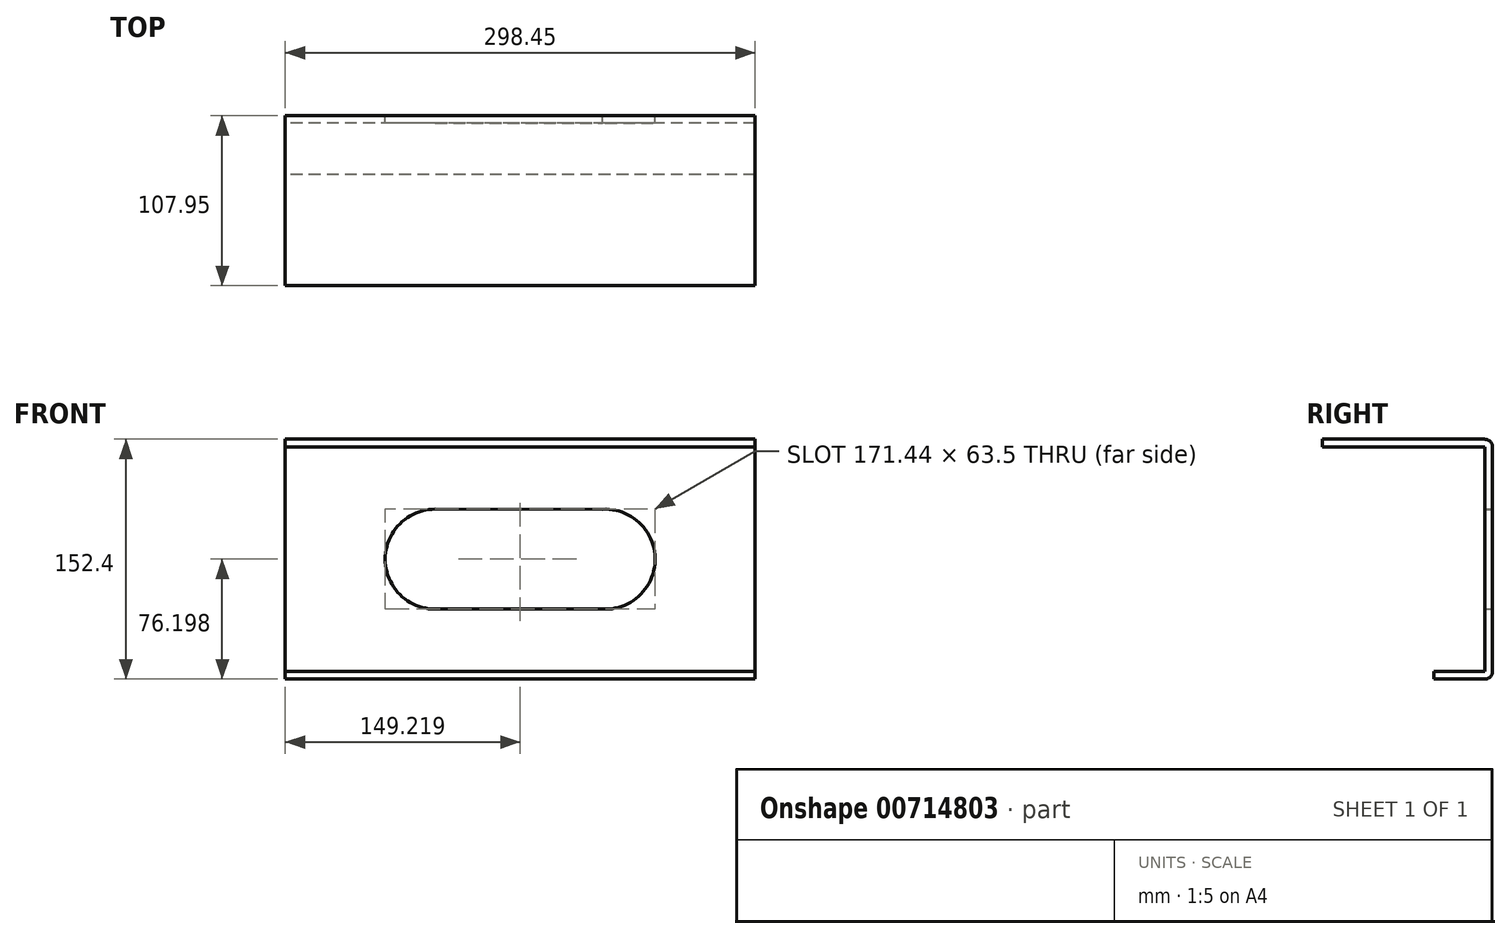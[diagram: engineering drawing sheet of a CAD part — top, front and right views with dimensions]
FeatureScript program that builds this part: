
annotation { "Feature Type Name" : "Feature", "Feature Type Description" : "" }
export const myFeature = defineFeature(function(context is Context, id is Id, definition is map)
    precondition{}
    {
        {
            var Q0;
            Q0=qCreatedBy(makeId("Right.planeOp"),FACE);
            var sketch = newSketch(context, id + "F0", { "sketchPlane" : qUnion([Q0])});
            skLineSegment(sketch, "E0", {"start": v(0, 66.65) * mm, "end": v(0, -85.75) * mm});
            skLineSegment(sketch, "E1", {"start": v(0, -85.75) * mm, "end": v(-37.34, -85.75) * mm});
            skLineSegment(sketch, "E2", {"start": v(-37.34, -85.75) * mm, "end": v(-37.34, -80.98) * mm});
            skLineSegment(sketch, "E3", {"start": v(-37.34, -80.98) * mm, "end": v(-4.78, -80.98) * mm});
            skLineSegment(sketch, "E4", {"start": v(-4.78, -80.98) * mm, "end": v(-4.78, 61.87) * mm});
            skLineSegment(sketch, "E5", {"start": v(-4.78, 61.87) * mm, "end": v(-107.95, 61.87) * mm});
            skLineSegment(sketch, "E6", {"start": v(-107.95, 61.87) * mm, "end": v(-107.95, 66.65) * mm});
            skLineSegment(sketch, "E7", {"start": v(-107.95, 66.65) * mm, "end": v(0, 66.65) * mm});
            skSolve(sketch);
        }
        {
            var Q0;
            Q0=makeQuery(id+"F0.imprint","IMPRINT",FACE,{"disambiguationData":[TD([[makeQuery(id+"F0.imprint","IMPRINT",EDGE,{"derivedFrom":sQuery(id+"F0.wireOp",EDGE,"E0")}),-1.0]])]});
            extrude(context, id + "F1", {"entities" : qUnion([Q0]), "depth" : 298.45 * mm, "offsetDistance" : 25.4 * mm});
        }
        {
            var Q0;
            Q0=makeQuery(id+"F1.opExtrude","SWEPT_EDGE",EDGE,{"disambiguationData":[OSD([sQuery(id+"F0.wireOp",EDGE,"E0"),sQuery(id+"F0.wireOp",EDGE,"E7")])]});
            var Q1;
            Q1=makeQuery(id+"F1.opExtrude","SWEPT_EDGE",EDGE,{"disambiguationData":[OSD([sQuery(id+"F0.wireOp",EDGE,"E0"),sQuery(id+"F0.wireOp",EDGE,"E1")])]});
            fillet(context, id + "F2", {"entities" : qUnion([Q0, Q1]), "radius" : 5.08 * mm, "tangentPropagation" : true, "allowEdgeOverflow" : false});
        }
        {
            var Q0;
            Q0=makeQuery(id+"F1.opExtrude","SWEPT_FACE",FACE,{"disambiguationData":[OSD([sQuery(id+"F0.wireOp",EDGE,"E0")])]});
            var sketch = newSketch(context, id + "F3", { "sketchPlane" : qUnion([Q0])});
            skLineSegment(sketch, "E8", {"start": v(-298.45, -9.55) * mm, "end": v(0, -9.55) * mm});
            skPoint(sketch, "E9", {"position": v(-203.2, -9.55) * mm});
            skPoint(sketch, "E10", {"position": v(-95.25, -9.55) * mm});
            skLineSegment(sketch, "E11", {"start": v(-149.23, 61.57) * mm, "end": v(-149.23, -80.67) * mm});
            skSolve(sketch);
        }
        {
            var Q0;
            Q0=sQuery(id+"F3.wireOp",VERTEX,"E9");
            var Q1;
            Q1=sQuery(id+"F3.wireOp",VERTEX,"E10");
            var Q2;
            Q2=makeQuery(id+"F1.opExtrude","SWEPT_BODY",BODY,{"disambiguationData":[OSD([sQuery(id+"F0.wireOp",EDGE,"E0"),sQuery(id+"F0.wireOp",EDGE,"E1"),sQuery(id+"F0.wireOp",EDGE,"E2"),sQuery(id+"F0.wireOp",EDGE,"E3"),sQuery(id+"F0.wireOp",EDGE,"E4"),sQuery(id+"F0.wireOp",EDGE,"E5"),sQuery(id+"F0.wireOp",EDGE,"E6"),sQuery(id+"F0.wireOp",EDGE,"E7")])]});
            hole(context, id + "F4", {"style" : HoleStyle.SIMPLE, "endStyle" : HoleEndStyle.THROUGH, "holeDiameter" : 63.5 * mm, "majorDiameter" : 6.35 * mm, "tappedDepth" : 110.49 * mm, "tapClearance" : 3, "startFromSketch" : true, "locations" : qUnion([Q0, Q1]), "scope" : qUnion([Q2])});
        }
        {
            var Q0;
            Q0=makeQuery(id+"F1.opExtrude","SWEPT_FACE",FACE,{"disambiguationData":[OSD([sQuery(id+"F0.wireOp",EDGE,"E0")])]});
            var sketch = newSketch(context, id + "F5", { "sketchPlane" : qUnion([Q0])});
            skLineSegment(sketch, "E12", {"start": v(-204.9, 22.15) * mm, "end": v(-95.26, 22.2) * mm});
            skLineSegment(sketch, "E13", {"start": v(-95.26, 22.2) * mm, "end": v(-95.26, -41.3) * mm});
            skLineSegment(sketch, "E14", {"start": v(-95.26, -41.3) * mm, "end": v(-203.2, -41.3) * mm});
            skLineSegment(sketch, "E15", {"start": v(-203.2, -41.3) * mm, "end": v(-204.9, 22.15) * mm});
            skSolve(sketch);
        }
        {
            var Q0;
            {var subQ6=sQuery(id+"F5.wireOp",EDGE,"E14");Q0=makeQuery(id+"F5.imprint","IMPRINT",FACE,{"disambiguationData":[TD([[makeQuery(id+"F5.imprint","IMPRINT",EDGE,{"derivedFrom":subQ6}),-1.0]])]});}
            extrude(context, id + "F6", {"entities" : qUnion([Q0]), "operationType" : NewBodyOperationType.REMOVE, "oppositeDirection" : true, "depth" : 25.4 * mm, "offsetDistance" : 25.4 * mm});
        }
    });
